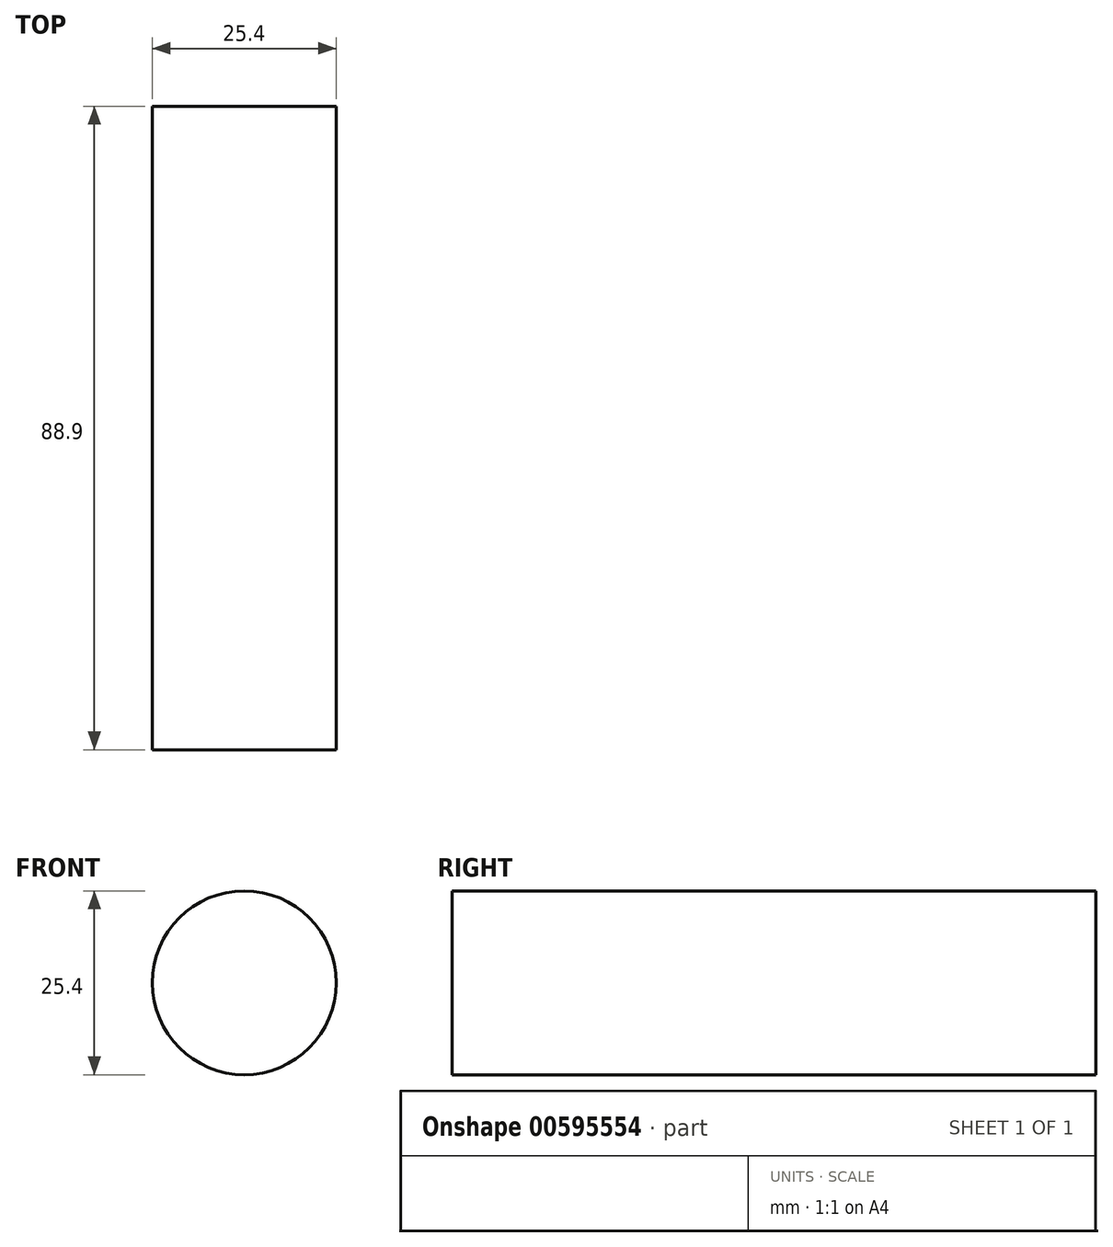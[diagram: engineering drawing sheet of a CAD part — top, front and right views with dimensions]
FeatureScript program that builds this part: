
annotation { "Feature Type Name" : "Feature", "Feature Type Description" : "" }
export const myFeature = defineFeature(function(context is Context, id is Id, definition is map)
    precondition{}
    {
        {
            var Q0;
            Q0=qCreatedBy(makeId("Front.planeOp"),FACE);
            var sketch = newSketch(context, id + "F0", { "sketchPlane" : qUnion([Q0])});
            skCircle(sketch, "E0", {"center": v(0, 0) * mm, "radius": 12.7 * mm});
            skSolve(sketch);
        }
        {
            var Q0;
            Q0=makeQuery(id+"F0.imprint","IMPRINT",FACE,{"disambiguationData":[TD([[makeQuery(id+"F0.imprint","IMPRINT",EDGE,{"derivedFrom":sQuery(id+"F0.wireOp",EDGE,"E0")}),1.0]])]});
            extrude(context, id + "F1", {"entities" : qUnion([Q0]), "depth" : 88.9 * mm, "offsetDistance" : 25.4 * mm, "symmetric" : true});
        }
    });
